# Revit family: WIR-RME
name_source: partatom
category: Communication Devices
units: mm (PartAtom-declared; Revit-internal decimal feet)

## family parameters
Cut with Voids When Loaded = No
Host = Face
Maintain Annotation Orientation = No
OmniClass Number = 23.85.80.11.27
OmniClass Title = Lighting Controls
Part Type = Normal
Room Calculation Point = No
Round Connector Dimension = Use Diameter
Shared = Yes

## types (1)
- WIR-RME
    Assembly Code = D5090
    Certifications = UL E485482
2.4GHz Version - FCC: U.S. FCC Part 15.247 Class A: OUR-XBEE / OUR-XBEE PRO, Canada IC: 4214A-XBEE /
4214A-XBEE PRO, Europe CE: ETSI / ETSI
900MHz Version - FCC: U.S. FCC Part 15.247 Class A: MCQ-XB900HP
    Default Elevation = 48 "
    Description = Control Solutions' wiSCAPE External Fixture Module is a bidirectional
wireless RF device that allows an individual fixture to be managed, monitored
and metered. The universal voltage (110-480VAC) module provides ON/OFF
control and features an adaptable sink & source 0-10V output compatible with
all 2-wire dimming drivers and ballast.
Available in either 2.4GHz or 900MHz ISM (Industrial, Scientific and Medical)
radio versions, each wiSCAPE External Fixture Module transmits over the air
using military grade AES-128 (Advanced Encryption Standard) security. AES is
a powerful encryption method used in many data security applications.
The wiSCAPE External Fixture Module drastically simplifies control and
automation of projects, especially in retrofit environments. The module
connects to ANSI C136-41-2013 7-pin or 5-pin twist-lock receptacles. The
wiSCAPE wireless lighting control technology adapts easily to complex
automation situations for quick, simple and economical commissioning.
    Electrical Rating = Input: 120-480VAC, 16A Max, 50-60Hz
Output: 5A@120-347V, 3A@480V
Surge Withstand: 2000V
Peak Inrush: 160A for 2 ms Max
Standby Power (W):
120VAC: 1.2
277VAC: 1.5
347VAC: 1.5
480VAC:1.3
    Housing Material = Paint - Carbon Black
    Manufacturer = NX Lighting Controls
    Model = NX On-Fixture Module
    Product Features = On/Off lighting control with 0-10V full-range dimming
• Bidirectional wireless RF Mesh communications
• Compliant with ANSI C136-41 (7 & 5 pin) twist-lock receptacles
• Digital input available for motion sensor, switch or photocell control
• Includes built-in, internal on/off photocell
• Military grade AES-128 communication encryption
• Multi-level grouping and multiple scenarios
• Adjustable minimum and maximum dimming levels
• Programmable power-up state with peak shaving options
• Commercial-grade metering
• Complete integration with wiSCAPE software
    Type Comments = wiSCAPE® External Fixture Module
    URL = https://www.currentlighting.com
    Warranty = 5-Years Warranty

## geometry (parser evidence)
native form markers: Sweep x3
no freeform markers — native parametric forms only
